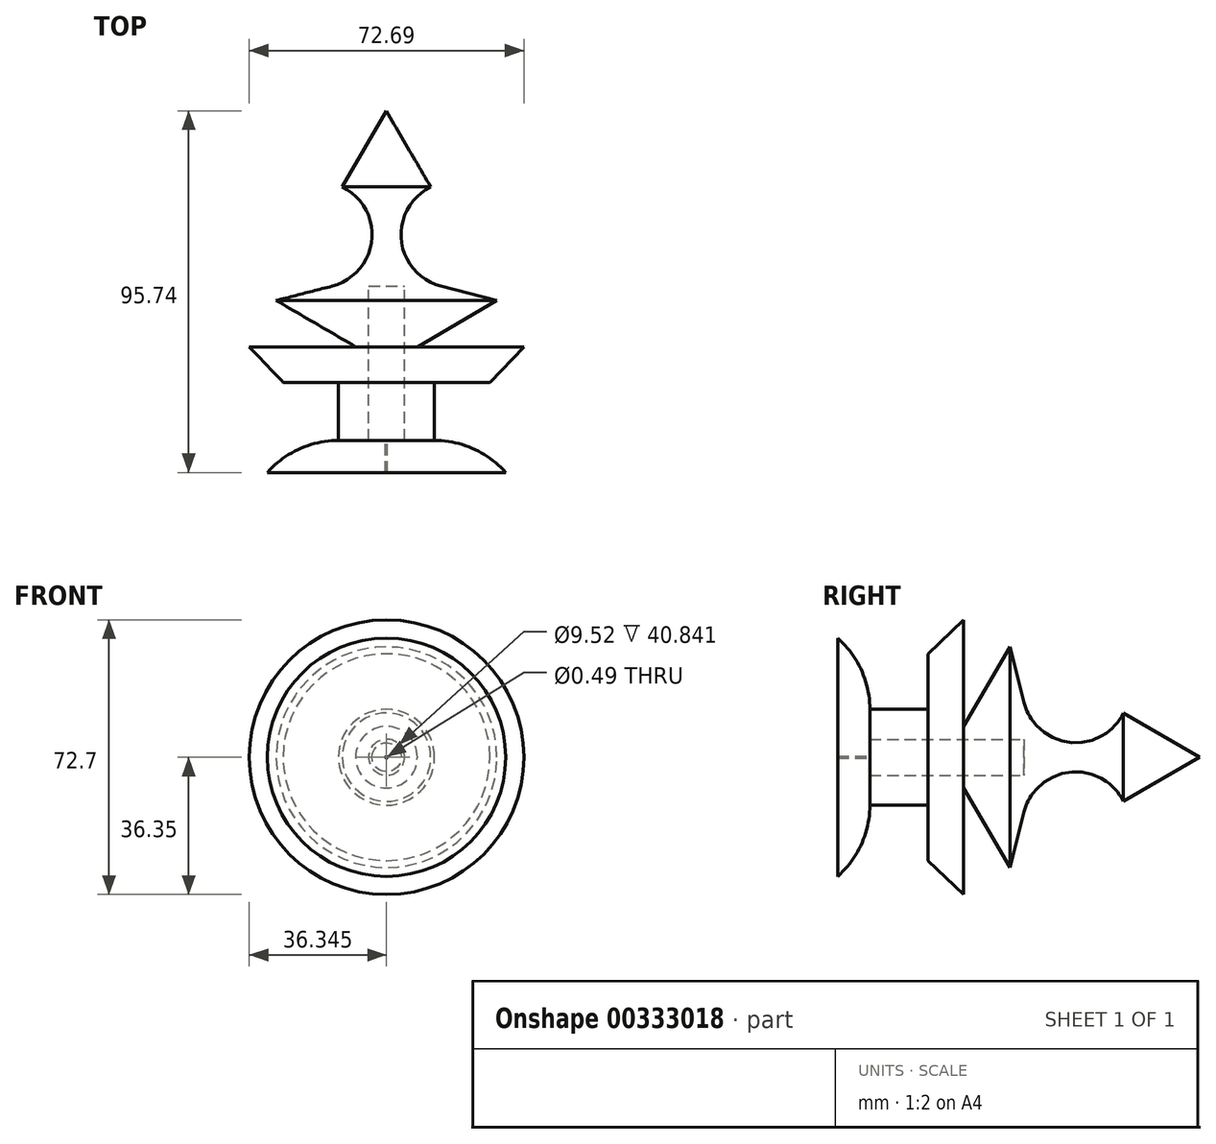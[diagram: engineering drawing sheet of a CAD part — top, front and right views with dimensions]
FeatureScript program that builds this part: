
annotation { "Feature Type Name" : "Feature", "Feature Type Description" : "" }
export const myFeature = defineFeature(function(context is Context, id is Id, definition is map)
    precondition{}
    {
        {
            var Q0;
            Q0=qCreatedBy(makeId("Top.planeOp"),FACE);
            var sketch = newSketch(context, id + "F0", { "sketchPlane" : qUnion([Q0])});
            skLineSegment(sketch, "E0.0", {"start": v(-0.24, 67.03) * mm, "end": v(11.46, 46.93) * mm});
            skPoint(sketch, "E0.0.midPoint", {"position": v(28.96, 16.86) * mm});
            skLineSegment(sketch, "E1", {"start": v(-0.24, 67.03) * mm, "end": v(-0.24, 20.65) * mm});
            skLineSegment(sketch, "E2", {"start": v(14.2, 20.65) * mm, "end": v(28.96, 16.86) * mm});
            skLineSegment(sketch, "E3", {"start": v(28.96, 16.86) * mm, "end": v(7.9, 4.6) * mm});
            skLineSegment(sketch, "E4", {"start": v(7.9, 4.6) * mm, "end": v(36.1, 4.6) * mm});
            skLineSegment(sketch, "E5", {"start": v(36.1, 4.6) * mm, "end": v(27.12, -4.81) * mm});
            skPoint(sketch, "E6.start.orphan", {"position": v(58.17, -33.3) * mm});
            skArc(sketch, "E7", {"start": v(11.46, 46.93) * mm, "mid": v(3.68, 32.84) * mm, "end": v(14.2, 20.65) * mm});
            skLineSegment(sketch, "E8.top", {"start": v(12.46, -4.81) * mm, "end": v(27.12, -4.81) * mm});
            skLineSegment(sketch, "E8.left", {"start": v(12.46, -20.2) * mm, "end": v(12.46, -4.81) * mm});
            skLineSegment(sketch, "E9.bottom", {"start": v(-0.24, 20.65) * mm, "end": v(4.52, 20.65) * mm});
            skLineSegment(sketch, "E9.right", {"start": v(4.52, 20.65) * mm, "end": v(4.52, -20.2) * mm});
            skLineSegment(sketch, "E10", {"start": v(12.46, -20.2) * mm, "end": v(4.52, -20.2) * mm});
            skArc(sketch, "E11", {"start": v(31.3, -28.71) * mm, "mid": v(22.8, -22.42) * mm, "end": v(12.46, -20.2) * mm});
            skLineSegment(sketch, "E12", {"start": v(4.52, -20.2) * mm, "end": v(0, -20.2) * mm});
            skLineSegment(sketch, "E13", {"start": v(0, -20.2) * mm, "end": v(0, -28.71) * mm});
            skLineSegment(sketch, "E14", {"start": v(0, -28.71) * mm, "end": v(31.3, -28.71) * mm});
            skSolve(sketch);
        }
        {
            var Q0;
            Q0=makeQuery(id+"F0.imprint","IMPRINT",FACE,{"disambiguationData":[TD([[makeQuery(id+"F0.imprint","IMPRINT",EDGE,{"derivedFrom":sQuery(id+"F0.wireOp",EDGE,"E0.0")}),-1.0]])]});
            var Q1;
            Q1=makeQuery(id+"F0.imprint","IMPRINT",FACE,{"disambiguationData":[TD([[makeQuery(id+"F0.imprint","IMPRINT",EDGE,{"derivedFrom":sQuery(id+"F0.wireOp",EDGE,"E10")}),1.0]])]});
            var Q2;
            Q2=sQuery(id+"F0.wireOp",EDGE,"E1");
            revolve(context, id + "F1", {"entities" : qUnion([Q0, Q1]), "axis" : qUnion([Q2]), "revolveType" : RevolveType.FULL});
        }
    });
